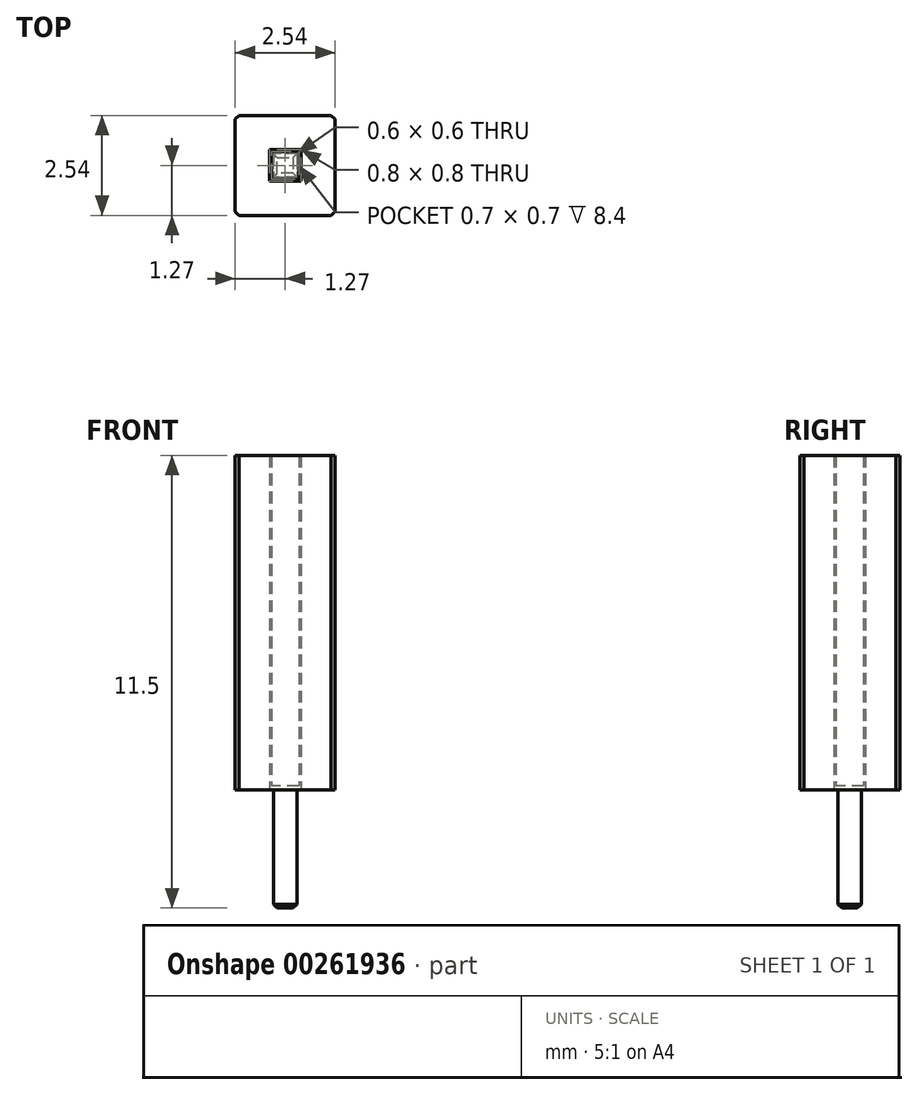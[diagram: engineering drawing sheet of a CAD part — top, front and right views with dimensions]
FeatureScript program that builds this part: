
annotation { "Feature Type Name" : "Feature", "Feature Type Description" : "" }
export const myFeature = defineFeature(function(context is Context, id is Id, definition is map)
    precondition{}
    {
        {
            var Q0;
            Q0=qCreatedBy(makeId("Top.planeOp"),FACE);
            var sketch = newSketch(context, id + "F0", { "sketchPlane" : qUnion([Q0])});
            skLineSegment(sketch, "E0.bottom", {"start": v(1.27, 1.27) * mm, "end": v(-1.27, 1.27) * mm});
            skLineSegment(sketch, "E0.top", {"start": v(1.27, -1.27) * mm, "end": v(-1.27, -1.27) * mm});
            skLineSegment(sketch, "E0.left", {"start": v(1.27, 1.27) * mm, "end": v(1.27, -1.27) * mm});
            skLineSegment(sketch, "E0.right", {"start": v(-1.27, 1.27) * mm, "end": v(-1.27, -1.27) * mm});
            skPoint(sketch, "E0.middle", {"position": v(0, 0) * mm});
            skLineSegment(sketch, "E1.bottom", {"start": v(0.4, 0.4) * mm, "end": v(-0.4, 0.4) * mm});
            skLineSegment(sketch, "E1.top", {"start": v(0.4, -0.4) * mm, "end": v(-0.4, -0.4) * mm});
            skLineSegment(sketch, "E1.left", {"start": v(0.4, 0.4) * mm, "end": v(0.4, -0.4) * mm});
            skLineSegment(sketch, "E1.right", {"start": v(-0.4, 0.4) * mm, "end": v(-0.4, -0.4) * mm});
            skSolve(sketch);
        }
        {
            var Q0;
            Q0=qSketchRegion(id+"F0",true);
            extrude(context, id + "F1", {"entities" : qUnion([Q0]), "depth" : 8.5 * mm});
        }
        {
            var Q0;
            Q0=makeQuery(id+"F1.opExtrude","SWEPT_EDGE",EDGE,{"disambiguationData":[OSD([sQuery(id+"F0.wireOp",EDGE,"E0.top"),sQuery(id+"F0.wireOp",EDGE,"E0.left")])]});
            var Q1;
            Q1=makeQuery(id+"F1.opExtrude","SWEPT_EDGE",EDGE,{"disambiguationData":[OSD([sQuery(id+"F0.wireOp",EDGE,"E0.top"),sQuery(id+"F0.wireOp",EDGE,"E0.right")])]});
            var Q2;
            Q2=makeQuery(id+"F1.opExtrude","SWEPT_EDGE",EDGE,{"disambiguationData":[OSD([sQuery(id+"F0.wireOp",EDGE,"E0.bottom"),sQuery(id+"F0.wireOp",EDGE,"E0.right")])]});
            var Q3;
            Q3=makeQuery(id+"F1.opExtrude","SWEPT_EDGE",EDGE,{"disambiguationData":[OSD([sQuery(id+"F0.wireOp",EDGE,"E0.bottom"),sQuery(id+"F0.wireOp",EDGE,"E0.left")])]});
            chamfer(context, id + "F2", {"entities" : qUnion([Q0, Q1, Q2, Q3]), "width" : 0.1 * mm, "tangentPropagation" : true});
        }
        {
            var Q0;
            Q0=qCreatedBy(makeId("Top.planeOp"),FACE);
            var sketch = newSketch(context, id + "F3", { "sketchPlane" : qUnion([Q0])});
            skLineSegment(sketch, "E2.bottom", {"start": v(0.3, 0.3) * mm, "end": v(-0.3, 0.3) * mm});
            skLineSegment(sketch, "E2.top", {"start": v(0.3, -0.3) * mm, "end": v(-0.3, -0.3) * mm});
            skLineSegment(sketch, "E2.left", {"start": v(0.3, 0.3) * mm, "end": v(0.3, -0.3) * mm});
            skLineSegment(sketch, "E2.right", {"start": v(-0.3, 0.3) * mm, "end": v(-0.3, -0.3) * mm});
            skPoint(sketch, "E2.middle", {"position": v(0, 0) * mm});
            skLineSegment(sketch, "E3.bottom", {"start": v(0.35, 0.35) * mm, "end": v(-0.35, 0.35) * mm});
            skLineSegment(sketch, "E3.top", {"start": v(0.35, -0.35) * mm, "end": v(-0.35, -0.35) * mm});
            skLineSegment(sketch, "E3.left", {"start": v(0.35, 0.35) * mm, "end": v(0.35, -0.35) * mm});
            skLineSegment(sketch, "E3.right", {"start": v(-0.35, 0.35) * mm, "end": v(-0.35, -0.35) * mm});
            skLineSegment(sketch, "E4.0", {"start": v(0.4, 0.4) * mm, "end": v(-0.4, 0.4) * mm});
            skLineSegment(sketch, "E4.1", {"start": v(-0.4, 0.4) * mm, "end": v(-0.4, -0.4) * mm});
            skLineSegment(sketch, "E4.2", {"start": v(0.4, 0.4) * mm, "end": v(0.4, -0.4) * mm});
            skLineSegment(sketch, "E4.3", {"start": v(0.4, -0.4) * mm, "end": v(-0.4, -0.4) * mm});
            skSolve(sketch);
        }
        {
            var Q0;
            Q0=makeQuery(id+"F3.imprint","IMPRINT",FACE,{"disambiguationData":[TD([[makeQuery(id+"F3.imprint","IMPRINT",EDGE,{"derivedFrom":sQuery(id+"F3.wireOp",EDGE,"E3.bottom")}),-1.0]])]});
            var Q1;
            Q1=makeQuery(id+"F1.opExtrude","CAP_FACE",FACE,{"disambiguationData":[OSD([sQuery(id+"F0.wireOp",EDGE,"E0.bottom"),sQuery(id+"F0.wireOp",EDGE,"E0.top"),sQuery(id+"F0.wireOp",EDGE,"E0.left"),sQuery(id+"F0.wireOp",EDGE,"E0.right"),sQuery(id+"F0.wireOp",EDGE,"E1.bottom"),sQuery(id+"F0.wireOp",EDGE,"E1.top"),sQuery(id+"F0.wireOp",EDGE,"E1.left"),sQuery(id+"F0.wireOp",EDGE,"E1.right")])],"isStart":false});
            extrude(context, id + "F4", {"entities" : qUnion([Q0]), "endBound" : BoundingType.UP_TO_SURFACE, "endBoundEntityFace" : qUnion([Q1]), "depth" : 25 * mm});
        }
        {
            var Q0;
            Q0=makeQuery(id+"F3.imprint","IMPRINT",FACE,{"disambiguationData":[TD([[makeQuery(id+"F3.imprint","IMPRINT",EDGE,{"derivedFrom":sQuery(id+"F3.wireOp",EDGE,"E2.bottom")}),-1.0]])]});
            extrude(context, id + "F5", {"entities" : qUnion([Q0]), "operationType" : NewBodyOperationType.ADD, "depth" : 0.1 * mm});
        }
        {
            var Q0;
            Q0=makeQuery(id+"F3.imprint","IMPRINT",FACE,{"disambiguationData":[TD([[makeQuery(id+"F3.imprint","IMPRINT",EDGE,{"derivedFrom":sQuery(id+"F3.wireOp",EDGE,"E2.bottom")}),1.0]])]});
            extrude(context, id + "F6", {"entities" : qUnion([Q0]), "operationType" : NewBodyOperationType.ADD, "oppositeDirection" : true, "depth" : 3 * mm, "hasSecondDirection" : true, "secondDirectionOppositeDirection" : false, "secondDirectionDepth" : 0.1 * mm});
        }
        {
            var Q0;
            Q0=makeQuery(id+"F6.opExtrude","CAP_FACE",FACE,{"disambiguationData":[OSD([sQuery(id+"F3.wireOp",EDGE,"E2.bottom"),sQuery(id+"F3.wireOp",EDGE,"E2.top"),sQuery(id+"F3.wireOp",EDGE,"E2.left"),sQuery(id+"F3.wireOp",EDGE,"E2.right")])],"isStart":false});
            chamfer(context, id + "F7", {"entities" : qUnion([Q0]), "width" : 0.1 * mm, "tangentPropagation" : true});
        }
    });
